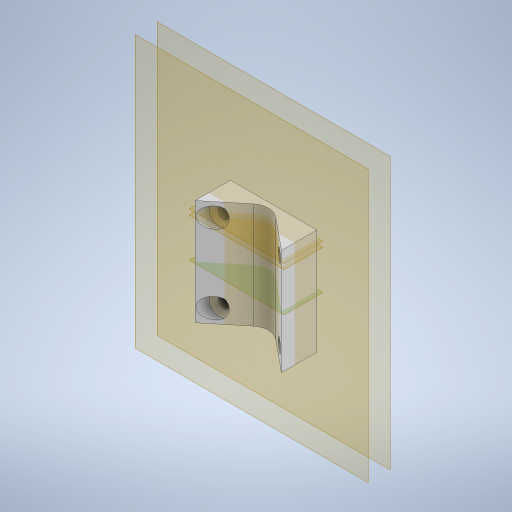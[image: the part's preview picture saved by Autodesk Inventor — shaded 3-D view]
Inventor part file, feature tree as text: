
AUTODESK INVENTOR PART (.ipt)
format: ipt  version: 2024.2 (Build 282272000, 272)  size: 308,736 bytes
history: native  units: mm
features: other x10, sketch x4, extrude x2, revolve x2, mirror x1, reference x1, projected_geometry x1
ambient origin geometry x8: Origin, YZ Plane, XZ Plane, XY Plane, X Axis, Y Axis, Z Axis, Center Point
bodies: Body1 (feature_tree)
feature tree (21):
  other  "Твердое тело1"
  other  "РабПлоскость1"
  extrude  "Выдавливание1"  Depth=3.0mm
  extrude  "Выдавливание2"  Depth=3.0mm
  other  "Сопряжение грани1"
  other  "РабПлоскость6"
  other  "РабПлоскость3"
  revolve  "Вращение1"
  revolve  "Вращение2"
  other  "РабПлоскость4"
  mirror  "Зеркальное отражение1"
  sketch  "Эскиз1"
  reference  "Ссылка1"
  sketch  "Эскиз2"
  other  "РабПлоскость2"
  sketch  "Эскиз3"
  sketch  "Эскиз4"
  projected_geometry  "Спроецированная петля1"
  other  "<userpath>\Documents\Artist\3D\каретка.iam"
  other  "каретка.iam"
  other  "ANY:5"
